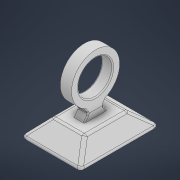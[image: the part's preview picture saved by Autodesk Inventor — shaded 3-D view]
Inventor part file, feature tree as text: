
AUTODESK INVENTOR PART (.ipt)
format: ipt  version: 2021 (Build 250183000, 183)  size: 312,832 bytes
history: native  units: mm
features: sketch x7, fillet x4, plane x3, loft x3, extrude x1, hole x1, other x1
ambient origin geometry x8: Origin, YZ Plane, XZ Plane, XY Plane, X Axis, Y Axis, Z Axis, Center Point
bodies: Solid1 (feature_tree)
feature tree (20):
  sketch  "Sketch1"  dims[d0=15.0mm d1=20.0mm d2=4.0mm d5=7.5mm]
  plane  "Work Plane1"
  loft  "Loft1"
  fillet  "Fillet1"  Radius=4.0mm
  fillet  "Fillet2"  Radius=7.5mm
  sketch  "Sketch3"  dims[d9=0.0mm d10=90.0deg d11=1.0mm d12=0.5mm]
  plane  "Work Plane2"
  sketch  "Sketch4"  dims[d15=2.634mm d16=5.298mm]
  plane  "Work Plane3"
  sketch  "Sketch5"  dims[d17=1.5mm d21=2.634mm d22=3.298mm]
  loft  "Loft2"
  loft  "Loft3"
  fillet  "Fillet3"  Radius=0.5mm
  extrude  "Extrusion1"  Depth=2.634mm
  hole  "Hole1"  [1 undecoded]
  fillet  "Fillet4"  Radius=3.298mm
  sketch  "Sketch2"  dims[d6=10.0mm d7=0.0mm d8=90.0deg]
  other  "Edges1"
  sketch  "Sketch6"  dims[d23=1.5mm]
  sketch  "Sketch7"  dims[d24=2.828mm d26=2.634mm d27=5.298mm d28=0.0mm d29=90.0deg d30=0.0mm d31=90.0deg d32=0.0mm d33=90.0deg d34=0.0mm d35=90.0deg d36=0.25mm d37=5.0mm d38=11.3mm d39=2.634mm d40=0.0mm d41=1.5mm d42=5.0mm d43=8.0mm d44=6.0mm d45=4.0mm d46=2.0mm d47=90.0deg d48=8.0mm d49=20.594885mm d50=0.25mm]
note: 1 required parameter value undecoded (feature->parameter linkage not recoverable at this tier; creation-order binding heuristic only, values carry confidence <= 0.55)
